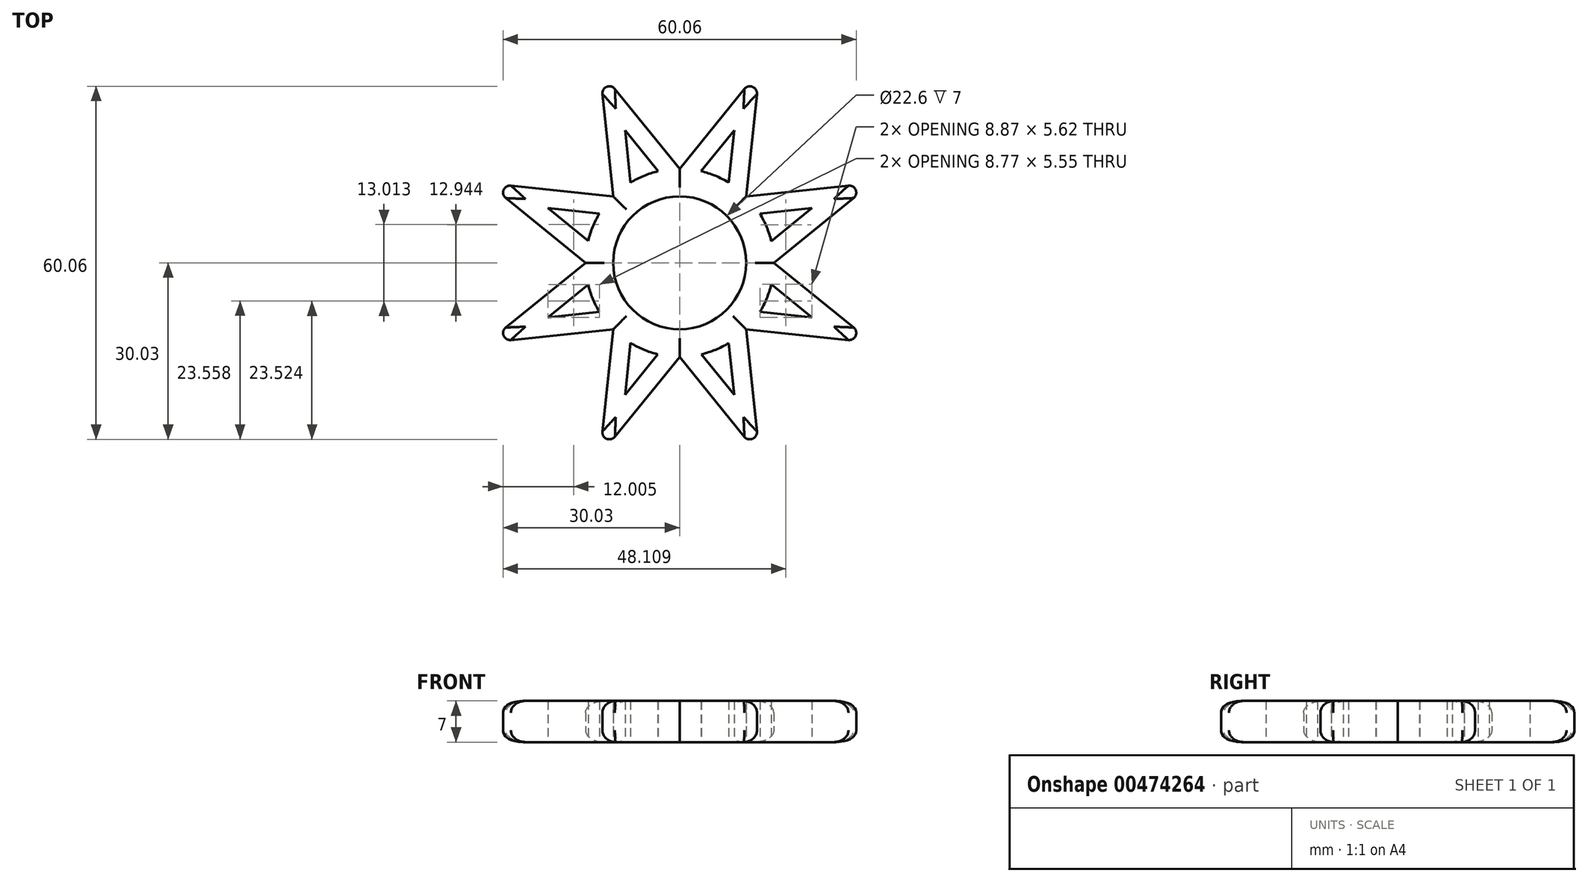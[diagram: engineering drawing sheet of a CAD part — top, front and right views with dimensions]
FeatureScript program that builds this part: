
annotation { "Feature Type Name" : "Feature", "Feature Type Description" : "" }
export const myFeature = defineFeature(function(context is Context, id is Id, definition is map)
    precondition{}
    {
        {
            var Q0;
            Q0=qCreatedBy(makeId("Top.planeOp"),FACE);
            var sketch = newSketch(context, id + "F0", { "sketchPlane" : qUnion([Q0])});
            skCircle(sketch, "E0", {"center": v(0, 0) * mm, "radius": 11.3 * mm});
            skCircle(sketch, "E1", {"center": v(0, 0) * mm, "radius": 16 * mm});
            skCircle(sketch, "E2.cCircle", {"center": v(0, 0) * mm, "radius": 16 * mm, "construction": true});
            skLineSegment(sketch, "E2.0", {"start": v(6.63, -16) * mm, "end": v(-6.63, -16) * mm});
            skLineSegment(sketch, "E2.1", {"start": v(-6.63, -16) * mm, "end": v(-16, -6.63) * mm});
            skLineSegment(sketch, "E2.2", {"start": v(-16, -6.63) * mm, "end": v(-16, 6.63) * mm});
            skLineSegment(sketch, "E2.3", {"start": v(-16, 6.63) * mm, "end": v(-6.63, 16) * mm});
            skLineSegment(sketch, "E2.4", {"start": v(-6.63, 16) * mm, "end": v(6.63, 16) * mm});
            skLineSegment(sketch, "E2.5", {"start": v(6.63, 16) * mm, "end": v(16, 6.63) * mm});
            skLineSegment(sketch, "E2.6", {"start": v(16, 6.63) * mm, "end": v(16, -6.63) * mm});
            skLineSegment(sketch, "E2.7", {"start": v(16, -6.63) * mm, "end": v(6.63, -16) * mm});
            skPoint(sketch, "E2.0.midPoint", {"position": v(0, -16) * mm});
            skCircle(sketch, "E3.cCircle", {"center": v(0, 0) * mm, "radius": 32.73 * mm, "construction": true});
            skLineSegment(sketch, "E3.0", {"start": v(13.56, -32.73) * mm, "end": v(-13.56, -32.73) * mm});
            skLineSegment(sketch, "E3.1", {"start": v(-13.56, -32.73) * mm, "end": v(-32.73, -13.56) * mm});
            skLineSegment(sketch, "E3.2", {"start": v(-32.73, -13.56) * mm, "end": v(-32.73, 13.56) * mm});
            skLineSegment(sketch, "E3.3", {"start": v(-32.73, 13.56) * mm, "end": v(-13.56, 32.73) * mm});
            skLineSegment(sketch, "E3.4", {"start": v(-13.56, 32.73) * mm, "end": v(13.56, 32.73) * mm});
            skLineSegment(sketch, "E3.5", {"start": v(13.56, 32.73) * mm, "end": v(32.73, 13.56) * mm});
            skLineSegment(sketch, "E3.6", {"start": v(32.73, 13.56) * mm, "end": v(32.73, -13.56) * mm});
            skLineSegment(sketch, "E3.7", {"start": v(32.73, -13.56) * mm, "end": v(13.56, -32.73) * mm});
            skPoint(sketch, "E3.0.midPoint", {"position": v(0, -32.73) * mm});
            skLineSegment(sketch, "E4", {"start": v(0, 16) * mm, "end": v(13.56, 32.73) * mm});
            skLineSegment(sketch, "E5", {"start": v(13.56, 32.73) * mm, "end": v(11.31, 11.31) * mm});
            skLineSegment(sketch, "E6", {"start": v(11.31, 11.31) * mm, "end": v(32.73, 13.56) * mm});
            skLineSegment(sketch, "E7", {"start": v(32.73, 13.56) * mm, "end": v(16, 0) * mm});
            skLineSegment(sketch, "E8", {"start": v(16, 0) * mm, "end": v(32.73, -13.56) * mm});
            skLineSegment(sketch, "E9", {"start": v(32.73, -13.56) * mm, "end": v(11.31, -11.31) * mm});
            skLineSegment(sketch, "E10", {"start": v(11.31, -11.31) * mm, "end": v(13.56, -32.73) * mm});
            skLineSegment(sketch, "E11", {"start": v(13.56, -32.73) * mm, "end": v(0, -16) * mm});
            skLineSegment(sketch, "E12", {"start": v(0, -16) * mm, "end": v(-13.56, -32.73) * mm});
            skLineSegment(sketch, "E13", {"start": v(-11.31, -11.31) * mm, "end": v(-13.56, -32.73) * mm});
            skLineSegment(sketch, "E14", {"start": v(0, 16) * mm, "end": v(-13.56, 32.73) * mm});
            skLineSegment(sketch, "E15", {"start": v(-11.31, 11.31) * mm, "end": v(-13.56, 32.73) * mm});
            skLineSegment(sketch, "E16", {"start": v(-11.31, 11.31) * mm, "end": v(-32.73, 13.56) * mm});
            skLineSegment(sketch, "E17", {"start": v(-32.73, 13.56) * mm, "end": v(-16, 0) * mm});
            skLineSegment(sketch, "E18", {"start": v(-16, 0) * mm, "end": v(-32.73, -13.56) * mm});
            skLineSegment(sketch, "E19", {"start": v(-32.73, -13.56) * mm, "end": v(-11.31, -11.31) * mm});
            skCircle(sketch, "E20.cCircle", {"center": v(0, 0) * mm, "radius": 22.41 * mm, "construction": true});
            skLineSegment(sketch, "E20.0", {"start": v(9.28, -22.41) * mm, "end": v(-9.28, -22.41) * mm});
            skLineSegment(sketch, "E20.1", {"start": v(-9.28, -22.41) * mm, "end": v(-22.41, -9.28) * mm});
            skLineSegment(sketch, "E20.2", {"start": v(-22.41, -9.28) * mm, "end": v(-22.41, 9.28) * mm});
            skLineSegment(sketch, "E20.3", {"start": v(-22.41, 9.28) * mm, "end": v(-9.28, 22.41) * mm});
            skLineSegment(sketch, "E20.4", {"start": v(-9.28, 22.41) * mm, "end": v(9.28, 22.41) * mm});
            skLineSegment(sketch, "E20.5", {"start": v(9.28, 22.41) * mm, "end": v(22.41, 9.28) * mm});
            skLineSegment(sketch, "E20.6", {"start": v(22.41, 9.28) * mm, "end": v(22.41, -9.28) * mm});
            skLineSegment(sketch, "E20.7", {"start": v(22.41, -9.28) * mm, "end": v(9.28, -22.41) * mm});
            skPoint(sketch, "E20.0.midPoint", {"position": v(0, -22.41) * mm});
            skLineSegment(sketch, "E21", {"start": v(-1, 7.04) * mm, "end": v(-22.41, 9.28) * mm});
            skLineSegment(sketch, "E22", {"start": v(-22.41, 9.28) * mm, "end": v(-5.69, -4.27) * mm});
            skLineSegment(sketch, "E23", {"start": v(-5.69, 4.27) * mm, "end": v(-22.41, -9.28) * mm});
            skLineSegment(sketch, "E24", {"start": v(-22.41, -9.28) * mm, "end": v(-1, -7.04) * mm});
            skPoint(sketch, "E25.0.midPoint", {"position": v(4.27, -5.69) * mm});
            skLineSegment(sketch, "E26", {"start": v(4.27, -5.69) * mm, "end": v(-9.28, -22.41) * mm});
            skLineSegment(sketch, "E27", {"start": v(-7.04, -1) * mm, "end": v(-9.28, -22.41) * mm});
            skPoint(sketch, "E28.0.midPoint", {"position": v(-4.3, -5.69) * mm});
            skLineSegment(sketch, "E29", {"start": v(7.01, -1) * mm, "end": v(9.25, -22.41) * mm});
            skLineSegment(sketch, "E30", {"start": v(9.25, -22.41) * mm, "end": v(-4.3, -5.69) * mm});
            skLineSegment(sketch, "E31", {"start": v(5.79, 4.27) * mm, "end": v(22.51, -9.28) * mm});
            skLineSegment(sketch, "E32", {"start": v(22.51, -9.28) * mm, "end": v(1.1, -7.04) * mm});
            skLineSegment(sketch, "E33", {"start": v(1.1, 7.04) * mm, "end": v(22.51, 9.28) * mm});
            skLineSegment(sketch, "E34", {"start": v(22.51, 9.28) * mm, "end": v(5.79, -4.27) * mm});
            skLineSegment(sketch, "E35", {"start": v(4.27, 5.78) * mm, "end": v(-9.28, 22.5) * mm});
            skLineSegment(sketch, "E36", {"start": v(-7.04, 1.1) * mm, "end": v(-9.28, 22.5) * mm});
            skLineSegment(sketch, "E37", {"start": v(-4.3, 5.78) * mm, "end": v(9.25, 22.5) * mm});
            skLineSegment(sketch, "E38", {"start": v(9.25, 22.5) * mm, "end": v(7.01, 1.1) * mm});
            skSolve(sketch);
        }
        {
            var Q0;
            Q0=makeQuery(id+"F0.imprint","IMPRINT",FACE,{"disambiguationData":[TD([[makeQuery(id+"F0.imprint","IMPRINT",EDGE,{"derivedFrom":sQuery(id+"F0.wireOp",EDGE,"E0")}),-1.0]])]});
            var Q1;
            {var subQ3=sQuery(id+"F0.wireOp",EDGE,"E4");Q1=makeQuery(id+"F0.imprint","IMPRINT",FACE,{"disambiguationData":[TD([[makeQuery(id+"F0.imprint","IMPRINT",EDGE,{"derivedFrom":subQ3}),-1.0]])]});}
            var Q2;
            {var subQ5=sQuery(id+"F0.wireOp",EDGE,"E14");Q2=makeQuery(id+"F0.imprint","IMPRINT",FACE,{"disambiguationData":[TD([[makeQuery(id+"F0.imprint","IMPRINT",EDGE,{"derivedFrom":subQ5}),1.0]])]});}
            var Q3;
            {var subQ5=sQuery(id+"F0.wireOp",EDGE,"E16");Q3=makeQuery(id+"F0.imprint","IMPRINT",FACE,{"disambiguationData":[TD([[makeQuery(id+"F0.imprint","IMPRINT",EDGE,{"derivedFrom":subQ5}),1.0]])]});}
            var Q4;
            {var subQ5=sQuery(id+"F0.wireOp",EDGE,"E18");Q4=makeQuery(id+"F0.imprint","IMPRINT",FACE,{"disambiguationData":[TD([[makeQuery(id+"F0.imprint","IMPRINT",EDGE,{"derivedFrom":subQ5}),1.0]])]});}
            var Q5;
            {var subQ3=sQuery(id+"F0.wireOp",EDGE,"E12");Q5=makeQuery(id+"F0.imprint","IMPRINT",FACE,{"disambiguationData":[TD([[makeQuery(id+"F0.imprint","IMPRINT",EDGE,{"derivedFrom":subQ3}),-1.0]])]});}
            var Q6;
            {var subQ5=sQuery(id+"F0.wireOp",EDGE,"E10");Q6=makeQuery(id+"F0.imprint","IMPRINT",FACE,{"disambiguationData":[TD([[makeQuery(id+"F0.imprint","IMPRINT",EDGE,{"derivedFrom":subQ5}),-1.0]])]});}
            var Q7;
            {var subQ3=sQuery(id+"F0.wireOp",EDGE,"E8");Q7=makeQuery(id+"F0.imprint","IMPRINT",FACE,{"disambiguationData":[TD([[makeQuery(id+"F0.imprint","IMPRINT",EDGE,{"derivedFrom":subQ3}),-1.0]])]});}
            var Q8;
            {var subQ3=sQuery(id+"F0.wireOp",EDGE,"E6");Q8=makeQuery(id+"F0.imprint","IMPRINT",FACE,{"disambiguationData":[TD([[makeQuery(id+"F0.imprint","IMPRINT",EDGE,{"derivedFrom":subQ3}),-1.0]])]});}
            var Q9;
            {var subQ1=sQuery(id+"F0.wireOp",EDGE,"E0");var subQ6=sQuery(id+"F0.wireOp",EDGE,"E36");var subQ8=makeQuery(id+"F0.imprint","INTERSECT",VERTEX,{"derivedFrom":[subQ1,subQ6]});Q9=makeQuery(id+"F0.imprint","IMPRINT",FACE,{"disambiguationData":[TD([[makeQuery(id+"F0.imprint","IMPRINT",EDGE,{"disambiguationData":[TD([[subQ8,-1.0]])],"derivedFrom":subQ1}),-1.0]])]});}
            var Q10;
            {var subQ4=sQuery(id+"F0.wireOp",EDGE,"E0");var subQ6=sQuery(id+"F0.wireOp",EDGE,"E37");var subQ8=makeQuery(id+"F0.imprint","INTERSECT",VERTEX,{"derivedFrom":[subQ4,subQ6]});Q10=makeQuery(id+"F0.imprint","IMPRINT",FACE,{"disambiguationData":[TD([[makeQuery(id+"F0.imprint","IMPRINT",EDGE,{"disambiguationData":[TD([[subQ8,-1.0]])],"derivedFrom":subQ4}),-1.0]])]});}
            var Q11;
            {var subQ0=sQuery(id+"F0.wireOp",EDGE,"E33");var subQ1=sQuery(id+"F0.wireOp",EDGE,"E0");var subQ2=makeQuery(id+"F0.imprint","INTERSECT",VERTEX,{"derivedFrom":[subQ1,subQ0]});Q11=makeQuery(id+"F0.imprint","IMPRINT",FACE,{"disambiguationData":[TD([[makeQuery(id+"F0.imprint","IMPRINT",EDGE,{"disambiguationData":[TD([[subQ2,-1.0]])],"derivedFrom":subQ1}),-1.0]])]});}
            var Q12;
            {var subQ1=sQuery(id+"F0.wireOp",EDGE,"E0");var subQ6=sQuery(id+"F0.wireOp",EDGE,"E34");var subQ8=makeQuery(id+"F0.imprint","INTERSECT",VERTEX,{"derivedFrom":[subQ1,subQ6]});Q12=makeQuery(id+"F0.imprint","IMPRINT",FACE,{"disambiguationData":[TD([[makeQuery(id+"F0.imprint","IMPRINT",EDGE,{"disambiguationData":[TD([[subQ8,1.0]])],"derivedFrom":subQ1}),-1.0]])]});}
            var Q13;
            {var subQ0=sQuery(id+"F0.wireOp",EDGE,"E29");var subQ1=sQuery(id+"F0.wireOp",EDGE,"E0");var subQ2=makeQuery(id+"F0.imprint","INTERSECT",VERTEX,{"derivedFrom":[subQ1,subQ0]});Q13=makeQuery(id+"F0.imprint","IMPRINT",FACE,{"disambiguationData":[TD([[makeQuery(id+"F0.imprint","IMPRINT",EDGE,{"disambiguationData":[TD([[subQ2,-1.0]])],"derivedFrom":subQ1}),-1.0]])]});}
            var Q14;
            {var subQ0=sQuery(id+"F0.wireOp",EDGE,"E26");var subQ1=sQuery(id+"F0.wireOp",EDGE,"E0");var subQ2=makeQuery(id+"F0.imprint","INTERSECT",VERTEX,{"derivedFrom":[subQ1,subQ0]});Q14=makeQuery(id+"F0.imprint","IMPRINT",FACE,{"disambiguationData":[TD([[makeQuery(id+"F0.imprint","IMPRINT",EDGE,{"disambiguationData":[TD([[subQ2,-1.0]])],"derivedFrom":subQ1}),-1.0]])]});}
            var Q15;
            {var subQ0=sQuery(id+"F0.wireOp",EDGE,"E24");var subQ1=sQuery(id+"F0.wireOp",EDGE,"E0");var subQ2=makeQuery(id+"F0.imprint","INTERSECT",VERTEX,{"derivedFrom":[subQ1,subQ0]});Q15=makeQuery(id+"F0.imprint","IMPRINT",FACE,{"disambiguationData":[TD([[makeQuery(id+"F0.imprint","IMPRINT",EDGE,{"disambiguationData":[TD([[subQ2,-1.0]])],"derivedFrom":subQ1}),-1.0]])]});}
            var Q16;
            {var subQ4=sQuery(id+"F0.wireOp",EDGE,"E22");var subQ5=sQuery(id+"F0.wireOp",EDGE,"E0");var subQ6=makeQuery(id+"F0.imprint","INTERSECT",VERTEX,{"derivedFrom":[subQ5,subQ4]});Q16=makeQuery(id+"F0.imprint","IMPRINT",FACE,{"disambiguationData":[TD([[makeQuery(id+"F0.imprint","IMPRINT",EDGE,{"disambiguationData":[TD([[subQ6,-1.0]])],"derivedFrom":subQ5}),-1.0]])]});}
            var Q17;
            {var subQ1=sQuery(id+"F0.wireOp",EDGE,"E1");var subQ3=sQuery(id+"F0.wireOp",EDGE,"E22");var subQ4=makeQuery(id+"F0.imprint","INTERSECT",VERTEX,{"derivedFrom":[subQ1,subQ3]});Q17=makeQuery(id+"F0.imprint","IMPRINT",FACE,{"disambiguationData":[TD([[makeQuery(id+"F0.imprint","IMPRINT",EDGE,{"disambiguationData":[TD([[subQ4,1.0]])],"derivedFrom":subQ3}),-1.0]])]});}
            var Q18;
            {var subQ1=sQuery(id+"F0.wireOp",EDGE,"E1");var subQ3=sQuery(id+"F0.wireOp",EDGE,"E21");var subQ4=makeQuery(id+"F0.imprint","INTERSECT",VERTEX,{"derivedFrom":[subQ1,subQ3]});Q18=makeQuery(id+"F0.imprint","IMPRINT",FACE,{"disambiguationData":[TD([[makeQuery(id+"F0.imprint","IMPRINT",EDGE,{"disambiguationData":[TD([[subQ4,-1.0]])],"derivedFrom":subQ3}),-1.0]])]});}
            var Q19;
            {var subQ1=sQuery(id+"F0.wireOp",EDGE,"E1");var subQ3=sQuery(id+"F0.wireOp",EDGE,"E36");var subQ4=makeQuery(id+"F0.imprint","INTERSECT",VERTEX,{"derivedFrom":[subQ1,subQ3]});Q19=makeQuery(id+"F0.imprint","IMPRINT",FACE,{"disambiguationData":[TD([[makeQuery(id+"F0.imprint","IMPRINT",EDGE,{"disambiguationData":[TD([[subQ4,-1.0]])],"derivedFrom":subQ3}),1.0]])]});}
            var Q20;
            {var subQ1=sQuery(id+"F0.wireOp",EDGE,"E1");var subQ3=sQuery(id+"F0.wireOp",EDGE,"E35");var subQ4=makeQuery(id+"F0.imprint","INTERSECT",VERTEX,{"derivedFrom":[subQ1,subQ3]});Q20=makeQuery(id+"F0.imprint","IMPRINT",FACE,{"disambiguationData":[TD([[makeQuery(id+"F0.imprint","IMPRINT",EDGE,{"disambiguationData":[TD([[subQ4,-1.0]])],"derivedFrom":subQ3}),-1.0]])]});}
            var Q21;
            {var subQ1=sQuery(id+"F0.wireOp",EDGE,"E1");var subQ3=sQuery(id+"F0.wireOp",EDGE,"E37");var subQ4=makeQuery(id+"F0.imprint","INTERSECT",VERTEX,{"derivedFrom":[subQ1,subQ3]});Q21=makeQuery(id+"F0.imprint","IMPRINT",FACE,{"disambiguationData":[TD([[makeQuery(id+"F0.imprint","IMPRINT",EDGE,{"disambiguationData":[TD([[subQ4,-1.0]])],"derivedFrom":subQ3}),1.0]])]});}
            var Q22;
            {var subQ1=sQuery(id+"F0.wireOp",EDGE,"E1");var subQ3=sQuery(id+"F0.wireOp",EDGE,"E38");var subQ4=makeQuery(id+"F0.imprint","INTERSECT",VERTEX,{"derivedFrom":[subQ1,subQ3]});Q22=makeQuery(id+"F0.imprint","IMPRINT",FACE,{"disambiguationData":[TD([[makeQuery(id+"F0.imprint","IMPRINT",EDGE,{"disambiguationData":[TD([[subQ4,1.0]])],"derivedFrom":subQ3}),1.0]])]});}
            var Q23;
            {var subQ0=sQuery(id+"F0.wireOp",EDGE,"E20.5");var subQ1=sQuery(id+"F0.wireOp",EDGE,"E20.4");var subQ2=makeQuery(id+"F0.imprint","INTERSECT",VERTEX,{"derivedFrom":[subQ1,subQ0]});Q23=makeQuery(id+"F0.imprint","IMPRINT",FACE,{"disambiguationData":[TD([[makeQuery(id+"F0.imprint","IMPRINT",EDGE,{"disambiguationData":[TD([[subQ2,1.0]])],"derivedFrom":subQ1}),-1.0]])]});}
            var Q24;
            {var subQ1=sQuery(id+"F0.wireOp",EDGE,"E1");var subQ3=sQuery(id+"F0.wireOp",EDGE,"E33");var subQ4=makeQuery(id+"F0.imprint","INTERSECT",VERTEX,{"derivedFrom":[subQ1,subQ3]});Q24=makeQuery(id+"F0.imprint","IMPRINT",FACE,{"disambiguationData":[TD([[makeQuery(id+"F0.imprint","IMPRINT",EDGE,{"disambiguationData":[TD([[subQ4,-1.0]])],"derivedFrom":subQ3}),1.0]])]});}
            var Q25;
            {var subQ1=sQuery(id+"F0.wireOp",EDGE,"E1");var subQ3=sQuery(id+"F0.wireOp",EDGE,"E34");var subQ4=makeQuery(id+"F0.imprint","INTERSECT",VERTEX,{"derivedFrom":[subQ1,subQ3]});Q25=makeQuery(id+"F0.imprint","IMPRINT",FACE,{"disambiguationData":[TD([[makeQuery(id+"F0.imprint","IMPRINT",EDGE,{"disambiguationData":[TD([[subQ4,1.0]])],"derivedFrom":subQ3}),1.0]])]});}
            var Q26;
            {var subQ1=sQuery(id+"F0.wireOp",EDGE,"E1");var subQ3=sQuery(id+"F0.wireOp",EDGE,"E31");var subQ4=makeQuery(id+"F0.imprint","INTERSECT",VERTEX,{"derivedFrom":[subQ1,subQ3]});Q26=makeQuery(id+"F0.imprint","IMPRINT",FACE,{"disambiguationData":[TD([[makeQuery(id+"F0.imprint","IMPRINT",EDGE,{"disambiguationData":[TD([[subQ4,-1.0]])],"derivedFrom":subQ3}),1.0]])]});}
            var Q27;
            {var subQ1=sQuery(id+"F0.wireOp",EDGE,"E1");var subQ3=sQuery(id+"F0.wireOp",EDGE,"E32");var subQ4=makeQuery(id+"F0.imprint","INTERSECT",VERTEX,{"derivedFrom":[subQ1,subQ3]});Q27=makeQuery(id+"F0.imprint","IMPRINT",FACE,{"disambiguationData":[TD([[makeQuery(id+"F0.imprint","IMPRINT",EDGE,{"disambiguationData":[TD([[subQ4,1.0]])],"derivedFrom":subQ3}),1.0]])]});}
            var Q28;
            {var subQ1=sQuery(id+"F0.wireOp",EDGE,"E1");var subQ3=sQuery(id+"F0.wireOp",EDGE,"E29");var subQ4=makeQuery(id+"F0.imprint","INTERSECT",VERTEX,{"derivedFrom":[subQ1,subQ3]});Q28=makeQuery(id+"F0.imprint","IMPRINT",FACE,{"disambiguationData":[TD([[makeQuery(id+"F0.imprint","IMPRINT",EDGE,{"disambiguationData":[TD([[subQ4,-1.0]])],"derivedFrom":subQ3}),1.0]])]});}
            var Q29;
            {var subQ1=sQuery(id+"F0.wireOp",EDGE,"E1");var subQ3=sQuery(id+"F0.wireOp",EDGE,"E30");var subQ4=makeQuery(id+"F0.imprint","INTERSECT",VERTEX,{"derivedFrom":[subQ1,subQ3]});Q29=makeQuery(id+"F0.imprint","IMPRINT",FACE,{"disambiguationData":[TD([[makeQuery(id+"F0.imprint","IMPRINT",EDGE,{"disambiguationData":[TD([[subQ4,1.0]])],"derivedFrom":subQ3}),1.0]])]});}
            var Q30;
            {var subQ1=sQuery(id+"F0.wireOp",EDGE,"E1");var subQ3=sQuery(id+"F0.wireOp",EDGE,"E26");var subQ4=makeQuery(id+"F0.imprint","INTERSECT",VERTEX,{"derivedFrom":[subQ1,subQ3]});Q30=makeQuery(id+"F0.imprint","IMPRINT",FACE,{"disambiguationData":[TD([[makeQuery(id+"F0.imprint","IMPRINT",EDGE,{"disambiguationData":[TD([[subQ4,-1.0]])],"derivedFrom":subQ3}),1.0]])]});}
            var Q31;
            {var subQ1=sQuery(id+"F0.wireOp",EDGE,"E1");var subQ3=sQuery(id+"F0.wireOp",EDGE,"E27");var subQ4=makeQuery(id+"F0.imprint","INTERSECT",VERTEX,{"derivedFrom":[subQ1,subQ3]});Q31=makeQuery(id+"F0.imprint","IMPRINT",FACE,{"disambiguationData":[TD([[makeQuery(id+"F0.imprint","IMPRINT",EDGE,{"disambiguationData":[TD([[subQ4,-1.0]])],"derivedFrom":subQ3}),-1.0]])]});}
            var Q32;
            {var subQ1=sQuery(id+"F0.wireOp",EDGE,"E1");var subQ3=sQuery(id+"F0.wireOp",EDGE,"E24");var subQ4=makeQuery(id+"F0.imprint","INTERSECT",VERTEX,{"derivedFrom":[subQ1,subQ3]});Q32=makeQuery(id+"F0.imprint","IMPRINT",FACE,{"disambiguationData":[TD([[makeQuery(id+"F0.imprint","IMPRINT",EDGE,{"disambiguationData":[TD([[subQ4,1.0]])],"derivedFrom":subQ3}),-1.0]])]});}
            var Q33;
            {var subQ1=sQuery(id+"F0.wireOp",EDGE,"E1");var subQ3=sQuery(id+"F0.wireOp",EDGE,"E23");var subQ4=makeQuery(id+"F0.imprint","INTERSECT",VERTEX,{"derivedFrom":[subQ1,subQ3]});Q33=makeQuery(id+"F0.imprint","IMPRINT",FACE,{"disambiguationData":[TD([[makeQuery(id+"F0.imprint","IMPRINT",EDGE,{"disambiguationData":[TD([[subQ4,-1.0]])],"derivedFrom":subQ3}),-1.0]])]});}
            var Q34;
            {var subQ1=sQuery(id+"F0.wireOp",EDGE,"E2.1");var subQ3=sQuery(id+"F0.wireOp",EDGE,"E24");var subQ4=makeQuery(id+"F0.imprint","INTERSECT",VERTEX,{"derivedFrom":[subQ1,subQ3]});Q34=makeQuery(id+"F0.imprint","IMPRINT",FACE,{"disambiguationData":[TD([[makeQuery(id+"F0.imprint","IMPRINT",EDGE,{"disambiguationData":[TD([[subQ4,1.0]])],"derivedFrom":subQ1}),1.0]])]});}
            var Q35;
            {var subQ1=sQuery(id+"F0.wireOp",EDGE,"E2.1");var subQ3=sQuery(id+"F0.wireOp",EDGE,"E27");var subQ4=makeQuery(id+"F0.imprint","INTERSECT",VERTEX,{"derivedFrom":[subQ1,subQ3]});Q35=makeQuery(id+"F0.imprint","IMPRINT",FACE,{"disambiguationData":[TD([[makeQuery(id+"F0.imprint","IMPRINT",EDGE,{"disambiguationData":[TD([[subQ4,-1.0]])],"derivedFrom":subQ1}),1.0]])]});}
            var Q36;
            {var subQ0=sQuery(id+"F0.wireOp",EDGE,"E11");var subQ5=sQuery(id+"F0.wireOp",EDGE,"E20.0");var subQ6=makeQuery(id+"F0.imprint","INTERSECT",VERTEX,{"derivedFrom":[subQ0,subQ5]});Q36=makeQuery(id+"F0.imprint","IMPRINT",FACE,{"disambiguationData":[TD([[makeQuery(id+"F0.imprint","IMPRINT",EDGE,{"disambiguationData":[TD([[subQ6,1.0]])],"derivedFrom":subQ5}),-1.0]])]});}
            var Q37;
            {var subQ0=sQuery(id+"F0.wireOp",EDGE,"E20.7");var subQ1=sQuery(id+"F0.wireOp",EDGE,"E20.6");var subQ2=makeQuery(id+"F0.imprint","INTERSECT",VERTEX,{"derivedFrom":[subQ1,subQ0]});Q37=makeQuery(id+"F0.imprint","IMPRINT",FACE,{"disambiguationData":[TD([[makeQuery(id+"F0.imprint","IMPRINT",EDGE,{"disambiguationData":[TD([[subQ2,1.0]])],"derivedFrom":subQ1}),-1.0]])]});}
            var Q38;
            {var subQ0=sQuery(id+"F0.wireOp",EDGE,"E7");var subQ5=sQuery(id+"F0.wireOp",EDGE,"E20.6");var subQ6=makeQuery(id+"F0.imprint","INTERSECT",VERTEX,{"derivedFrom":[subQ0,subQ5]});Q38=makeQuery(id+"F0.imprint","IMPRINT",FACE,{"disambiguationData":[TD([[makeQuery(id+"F0.imprint","IMPRINT",EDGE,{"disambiguationData":[TD([[subQ6,1.0]])],"derivedFrom":subQ5}),-1.0]])]});}
            var Q39;
            {var subQ1=sQuery(id+"F0.wireOp",EDGE,"E2.2");var subQ3=sQuery(id+"F0.wireOp",EDGE,"E22");var subQ4=makeQuery(id+"F0.imprint","INTERSECT",VERTEX,{"derivedFrom":[subQ1,subQ3]});Q39=makeQuery(id+"F0.imprint","IMPRINT",FACE,{"disambiguationData":[TD([[makeQuery(id+"F0.imprint","IMPRINT",EDGE,{"disambiguationData":[TD([[subQ4,1.0]])],"derivedFrom":subQ1}),1.0]])]});}
            var Q40;
            {var subQ0=sQuery(id+"F0.wireOp",EDGE,"E20.4");var subQ1=sQuery(id+"F0.wireOp",EDGE,"E20.3");var subQ2=makeQuery(id+"F0.imprint","INTERSECT",VERTEX,{"derivedFrom":[subQ1,subQ0]});Q40=makeQuery(id+"F0.imprint","IMPRINT",FACE,{"disambiguationData":[TD([[makeQuery(id+"F0.imprint","IMPRINT",EDGE,{"disambiguationData":[TD([[subQ2,1.0]])],"derivedFrom":subQ1}),-1.0]])]});}
            var Q41;
            {var subQ0=sQuery(id+"F0.wireOp",EDGE,"E20.4");var subQ1=sQuery(id+"F0.wireOp",EDGE,"E20.3");var subQ2=makeQuery(id+"F0.imprint","INTERSECT",VERTEX,{"derivedFrom":[subQ1,subQ0]});Q41=makeQuery(id+"F0.imprint","IMPRINT",FACE,{"disambiguationData":[TD([[makeQuery(id+"F0.imprint","IMPRINT",EDGE,{"disambiguationData":[TD([[subQ2,1.0]])],"derivedFrom":subQ1}),1.0]])]});}
            var Q42;
            {var subQ0=sQuery(id+"F0.wireOp",EDGE,"E20.4");var subQ1=sQuery(id+"F0.wireOp",EDGE,"E4");var subQ2=makeQuery(id+"F0.imprint","INTERSECT",VERTEX,{"derivedFrom":[subQ1,subQ0]});Q42=makeQuery(id+"F0.imprint","IMPRINT",FACE,{"disambiguationData":[TD([[makeQuery(id+"F0.imprint","IMPRINT",EDGE,{"disambiguationData":[TD([[subQ2,-1.0]])],"derivedFrom":subQ0}),1.0]])]});}
            var Q43;
            {var subQ0=sQuery(id+"F0.wireOp",EDGE,"E20.6");var subQ1=sQuery(id+"F0.wireOp",EDGE,"E20.5");var subQ2=makeQuery(id+"F0.imprint","INTERSECT",VERTEX,{"derivedFrom":[subQ1,subQ0]});Q43=makeQuery(id+"F0.imprint","IMPRINT",FACE,{"disambiguationData":[TD([[makeQuery(id+"F0.imprint","IMPRINT",EDGE,{"disambiguationData":[TD([[subQ2,1.0]])],"derivedFrom":subQ1}),1.0]])]});}
            var Q44;
            {var subQ1=sQuery(id+"F0.wireOp",EDGE,"E20.6");var subQ6=sQuery(id+"F0.wireOp",EDGE,"E8");var subQ9=makeQuery(id+"F0.imprint","INTERSECT",VERTEX,{"derivedFrom":[subQ6,subQ1]});Q44=makeQuery(id+"F0.imprint","IMPRINT",FACE,{"disambiguationData":[TD([[makeQuery(id+"F0.imprint","IMPRINT",EDGE,{"disambiguationData":[TD([[subQ9,-1.0]])],"derivedFrom":subQ1}),1.0]])]});}
            extrude(context, id + "F1", {"entities" : qUnion([Q0, Q1, Q2, Q3, Q4, Q5, Q6, Q7, Q8, Q9, Q10, Q11, Q12, Q13, Q14, Q15, Q16, Q17, Q18, Q19, Q20, Q21, Q22, Q23, Q24, Q25, Q26, Q27, Q28, Q29, Q30, Q31, Q32, Q33, Q34, Q35, Q36, Q37, Q38, Q39, Q40, Q41, Q42, Q43, Q44]), "depth" : 7 * mm});
        }
        {
            var Q0;
            Q0=makeQuery(id+"F1.opExtrude","CAP_EDGE",EDGE,{"disambiguationData":[OSD([sQuery(id+"F0.wireOp",EDGE,"E9")])],"isStart":false});
            var Q1;
            Q1=makeQuery(id+"F1.opExtrude","CAP_EDGE",EDGE,{"disambiguationData":[OSD([sQuery(id+"F0.wireOp",EDGE,"E10")])],"isStart":false});
            var Q2;
            Q2=makeQuery(id+"F1.opExtrude","CAP_EDGE",EDGE,{"disambiguationData":[OSD([sQuery(id+"F0.wireOp",EDGE,"E11")])],"isStart":false});
            var Q3;
            Q3=makeQuery(id+"F1.opExtrude","CAP_EDGE",EDGE,{"disambiguationData":[OSD([sQuery(id+"F0.wireOp",EDGE,"E12")])],"isStart":false});
            var Q4;
            Q4=makeQuery(id+"F1.opExtrude","CAP_EDGE",EDGE,{"disambiguationData":[OSD([sQuery(id+"F0.wireOp",EDGE,"E13")])],"isStart":false});
            var Q5;
            Q5=makeQuery(id+"F1.opExtrude","CAP_EDGE",EDGE,{"disambiguationData":[OSD([sQuery(id+"F0.wireOp",EDGE,"E19")])],"isStart":false});
            var Q6;
            Q6=makeQuery(id+"F1.opExtrude","CAP_EDGE",EDGE,{"disambiguationData":[OSD([sQuery(id+"F0.wireOp",EDGE,"E18")])],"isStart":false});
            var Q7;
            Q7=makeQuery(id+"F1.opExtrude","CAP_EDGE",EDGE,{"disambiguationData":[OSD([sQuery(id+"F0.wireOp",EDGE,"E17")])],"isStart":false});
            var Q8;
            Q8=makeQuery(id+"F1.opExtrude","CAP_EDGE",EDGE,{"disambiguationData":[OSD([sQuery(id+"F0.wireOp",EDGE,"E16")])],"isStart":false});
            var Q9;
            Q9=makeQuery(id+"F1.opExtrude","CAP_EDGE",EDGE,{"disambiguationData":[OSD([sQuery(id+"F0.wireOp",EDGE,"E15")])],"isStart":false});
            var Q10;
            Q10=makeQuery(id+"F1.opExtrude","CAP_EDGE",EDGE,{"disambiguationData":[OSD([sQuery(id+"F0.wireOp",EDGE,"E14")])],"isStart":false});
            var Q11;
            Q11=makeQuery(id+"F1.opExtrude","CAP_EDGE",EDGE,{"disambiguationData":[OSD([sQuery(id+"F0.wireOp",EDGE,"E4")])],"isStart":false});
            var Q12;
            Q12=makeQuery(id+"F1.opExtrude","CAP_EDGE",EDGE,{"disambiguationData":[OSD([sQuery(id+"F0.wireOp",EDGE,"E5")])],"isStart":false});
            var Q13;
            Q13=makeQuery(id+"F1.opExtrude","CAP_EDGE",EDGE,{"disambiguationData":[OSD([sQuery(id+"F0.wireOp",EDGE,"E6")])],"isStart":false});
            var Q14;
            Q14=makeQuery(id+"F1.opExtrude","CAP_EDGE",EDGE,{"disambiguationData":[OSD([sQuery(id+"F0.wireOp",EDGE,"E7")])],"isStart":false});
            var Q15;
            Q15=makeQuery(id+"F1.opExtrude","CAP_EDGE",EDGE,{"disambiguationData":[OSD([sQuery(id+"F0.wireOp",EDGE,"E8")])],"isStart":false});
            fillet(context, id + "F2", {"entities" : qUnion([Q0, Q1, Q2, Q3, Q4, Q5, Q6, Q7, Q8, Q9, Q10, Q11, Q12, Q13, Q14, Q15]), "radius" : 2 * mm, "tangentPropagation" : true, "allowEdgeOverflow" : false});
        }
        {
            var Q0;
            Q0=makeQuery(id+"F1.opExtrude","CAP_EDGE",EDGE,{"disambiguationData":[OSD([sQuery(id+"F0.wireOp",EDGE,"E12")])],"isStart":true});
            var Q1;
            Q1=makeQuery(id+"F1.opExtrude","CAP_EDGE",EDGE,{"disambiguationData":[OSD([sQuery(id+"F0.wireOp",EDGE,"E11")])],"isStart":true});
            var Q2;
            Q2=makeQuery(id+"F1.opExtrude","CAP_EDGE",EDGE,{"disambiguationData":[OSD([sQuery(id+"F0.wireOp",EDGE,"E10")])],"isStart":true});
            var Q3;
            Q3=makeQuery(id+"F1.opExtrude","CAP_EDGE",EDGE,{"disambiguationData":[OSD([sQuery(id+"F0.wireOp",EDGE,"E9")])],"isStart":true});
            var Q4;
            Q4=makeQuery(id+"F1.opExtrude","CAP_EDGE",EDGE,{"disambiguationData":[OSD([sQuery(id+"F0.wireOp",EDGE,"E8")])],"isStart":true});
            var Q5;
            Q5=makeQuery(id+"F1.opExtrude","CAP_EDGE",EDGE,{"disambiguationData":[OSD([sQuery(id+"F0.wireOp",EDGE,"E7")])],"isStart":true});
            var Q6;
            Q6=makeQuery(id+"F1.opExtrude","CAP_EDGE",EDGE,{"disambiguationData":[OSD([sQuery(id+"F0.wireOp",EDGE,"E6")])],"isStart":true});
            var Q7;
            Q7=makeQuery(id+"F1.opExtrude","CAP_EDGE",EDGE,{"disambiguationData":[OSD([sQuery(id+"F0.wireOp",EDGE,"E5")])],"isStart":true});
            var Q8;
            Q8=makeQuery(id+"F1.opExtrude","CAP_EDGE",EDGE,{"disambiguationData":[OSD([sQuery(id+"F0.wireOp",EDGE,"E4")])],"isStart":true});
            var Q9;
            Q9=makeQuery(id+"F1.opExtrude","CAP_EDGE",EDGE,{"disambiguationData":[OSD([sQuery(id+"F0.wireOp",EDGE,"E14")])],"isStart":true});
            var Q10;
            Q10=makeQuery(id+"F1.opExtrude","CAP_EDGE",EDGE,{"disambiguationData":[OSD([sQuery(id+"F0.wireOp",EDGE,"E15")])],"isStart":true});
            var Q11;
            Q11=makeQuery(id+"F1.opExtrude","CAP_EDGE",EDGE,{"disambiguationData":[OSD([sQuery(id+"F0.wireOp",EDGE,"E16")])],"isStart":true});
            var Q12;
            Q12=makeQuery(id+"F1.opExtrude","CAP_EDGE",EDGE,{"disambiguationData":[OSD([sQuery(id+"F0.wireOp",EDGE,"E17")])],"isStart":true});
            var Q13;
            Q13=makeQuery(id+"F1.opExtrude","CAP_EDGE",EDGE,{"disambiguationData":[OSD([sQuery(id+"F0.wireOp",EDGE,"E18")])],"isStart":true});
            var Q14;
            Q14=makeQuery(id+"F1.opExtrude","CAP_EDGE",EDGE,{"disambiguationData":[OSD([sQuery(id+"F0.wireOp",EDGE,"E19")])],"isStart":true});
            var Q15;
            Q15=makeQuery(id+"F1.opExtrude","CAP_EDGE",EDGE,{"disambiguationData":[OSD([sQuery(id+"F0.wireOp",EDGE,"E13")])],"isStart":true});
            fillet(context, id + "F3", {"entities" : qUnion([Q0, Q1, Q2, Q3, Q4, Q5, Q6, Q7, Q8, Q9, Q10, Q11, Q12, Q13, Q14, Q15]), "radius" : 2 * mm, "tangentPropagation" : true, "allowEdgeOverflow" : false});
        }
        {
            var Q0;
            Q0=makeQuery(id+"F1.opExtrude","SWEPT_EDGE",EDGE,{"disambiguationData":[OSD([sQuery(id+"F0.wireOp",EDGE,"E3.0"),sQuery(id+"F0.wireOp",EDGE,"E3.1"),sQuery(id+"F0.wireOp",EDGE,"E12"),sQuery(id+"F0.wireOp",EDGE,"E13")])]});
            var Q1;
            Q1=makeQuery(id+"F3.opFillet","BLEND_EDGE",EDGE,{"blendedFrom":[makeQuery(id+"F1.opExtrude","CAP_EDGE",EDGE,{"disambiguationData":[OSD([sQuery(id+"F0.wireOp",EDGE,"E12")])],"isStart":true}),makeQuery(id+"F1.opExtrude","CAP_EDGE",EDGE,{"disambiguationData":[OSD([sQuery(id+"F0.wireOp",EDGE,"E13")])],"isStart":true})],"blendedInto":[]});
            var Q2;
            Q2=makeQuery(id+"F2.opFillet","BLEND_EDGE",EDGE,{"blendedFrom":[makeQuery(id+"F1.opExtrude","CAP_EDGE",EDGE,{"disambiguationData":[OSD([sQuery(id+"F0.wireOp",EDGE,"E12")])],"isStart":false}),makeQuery(id+"F1.opExtrude","CAP_EDGE",EDGE,{"disambiguationData":[OSD([sQuery(id+"F0.wireOp",EDGE,"E13")])],"isStart":false})],"blendedInto":[]});
            var Q3;
            Q3=makeQuery(id+"F1.opExtrude","SWEPT_EDGE",EDGE,{"disambiguationData":[OSD([sQuery(id+"F0.wireOp",EDGE,"E3.0"),sQuery(id+"F0.wireOp",EDGE,"E3.7"),sQuery(id+"F0.wireOp",EDGE,"E10"),sQuery(id+"F0.wireOp",EDGE,"E11")])]});
            var Q4;
            Q4=makeQuery(id+"F2.opFillet","BLEND_EDGE",EDGE,{"blendedFrom":[makeQuery(id+"F1.opExtrude","CAP_EDGE",EDGE,{"disambiguationData":[OSD([sQuery(id+"F0.wireOp",EDGE,"E10")])],"isStart":false}),makeQuery(id+"F1.opExtrude","CAP_EDGE",EDGE,{"disambiguationData":[OSD([sQuery(id+"F0.wireOp",EDGE,"E11")])],"isStart":false})],"blendedInto":[]});
            var Q5;
            Q5=makeQuery(id+"F3.opFillet","BLEND_EDGE",EDGE,{"blendedFrom":[makeQuery(id+"F1.opExtrude","CAP_EDGE",EDGE,{"disambiguationData":[OSD([sQuery(id+"F0.wireOp",EDGE,"E10")])],"isStart":true}),makeQuery(id+"F1.opExtrude","CAP_EDGE",EDGE,{"disambiguationData":[OSD([sQuery(id+"F0.wireOp",EDGE,"E11")])],"isStart":true})],"blendedInto":[]});
            var Q6;
            Q6=makeQuery(id+"F2.opFillet","BLEND_EDGE",EDGE,{"blendedFrom":[makeQuery(id+"F1.opExtrude","CAP_EDGE",EDGE,{"disambiguationData":[OSD([sQuery(id+"F0.wireOp",EDGE,"E8")])],"isStart":false}),makeQuery(id+"F1.opExtrude","CAP_EDGE",EDGE,{"disambiguationData":[OSD([sQuery(id+"F0.wireOp",EDGE,"E9")])],"isStart":false})],"blendedInto":[]});
            var Q7;
            Q7=makeQuery(id+"F1.opExtrude","SWEPT_EDGE",EDGE,{"disambiguationData":[OSD([sQuery(id+"F0.wireOp",EDGE,"E3.6"),sQuery(id+"F0.wireOp",EDGE,"E3.7"),sQuery(id+"F0.wireOp",EDGE,"E8"),sQuery(id+"F0.wireOp",EDGE,"E9")])]});
            var Q8;
            Q8=makeQuery(id+"F3.opFillet","BLEND_EDGE",EDGE,{"blendedFrom":[makeQuery(id+"F1.opExtrude","CAP_EDGE",EDGE,{"disambiguationData":[OSD([sQuery(id+"F0.wireOp",EDGE,"E8")])],"isStart":true}),makeQuery(id+"F1.opExtrude","CAP_EDGE",EDGE,{"disambiguationData":[OSD([sQuery(id+"F0.wireOp",EDGE,"E9")])],"isStart":true})],"blendedInto":[]});
            var Q9;
            Q9=makeQuery(id+"F1.opExtrude","SWEPT_EDGE",EDGE,{"disambiguationData":[OSD([sQuery(id+"F0.wireOp",EDGE,"E3.5"),sQuery(id+"F0.wireOp",EDGE,"E3.6"),sQuery(id+"F0.wireOp",EDGE,"E6"),sQuery(id+"F0.wireOp",EDGE,"E7")])]});
            var Q10;
            Q10=makeQuery(id+"F2.opFillet","BLEND_EDGE",EDGE,{"blendedFrom":[makeQuery(id+"F1.opExtrude","CAP_EDGE",EDGE,{"disambiguationData":[OSD([sQuery(id+"F0.wireOp",EDGE,"E6")])],"isStart":false}),makeQuery(id+"F1.opExtrude","CAP_EDGE",EDGE,{"disambiguationData":[OSD([sQuery(id+"F0.wireOp",EDGE,"E7")])],"isStart":false})],"blendedInto":[]});
            var Q11;
            Q11=makeQuery(id+"F3.opFillet","BLEND_EDGE",EDGE,{"blendedFrom":[makeQuery(id+"F1.opExtrude","CAP_EDGE",EDGE,{"disambiguationData":[OSD([sQuery(id+"F0.wireOp",EDGE,"E6")])],"isStart":true}),makeQuery(id+"F1.opExtrude","CAP_EDGE",EDGE,{"disambiguationData":[OSD([sQuery(id+"F0.wireOp",EDGE,"E7")])],"isStart":true})],"blendedInto":[]});
            var Q12;
            Q12=makeQuery(id+"F2.opFillet","BLEND_EDGE",EDGE,{"blendedFrom":[makeQuery(id+"F1.opExtrude","CAP_EDGE",EDGE,{"disambiguationData":[OSD([sQuery(id+"F0.wireOp",EDGE,"E4")])],"isStart":false}),makeQuery(id+"F1.opExtrude","CAP_EDGE",EDGE,{"disambiguationData":[OSD([sQuery(id+"F0.wireOp",EDGE,"E5")])],"isStart":false})],"blendedInto":[]});
            var Q13;
            Q13=makeQuery(id+"F1.opExtrude","SWEPT_EDGE",EDGE,{"disambiguationData":[OSD([sQuery(id+"F0.wireOp",EDGE,"E3.4"),sQuery(id+"F0.wireOp",EDGE,"E3.5"),sQuery(id+"F0.wireOp",EDGE,"E4"),sQuery(id+"F0.wireOp",EDGE,"E5")])]});
            var Q14;
            Q14=makeQuery(id+"F3.opFillet","BLEND_EDGE",EDGE,{"blendedFrom":[makeQuery(id+"F1.opExtrude","CAP_EDGE",EDGE,{"disambiguationData":[OSD([sQuery(id+"F0.wireOp",EDGE,"E4")])],"isStart":true}),makeQuery(id+"F1.opExtrude","CAP_EDGE",EDGE,{"disambiguationData":[OSD([sQuery(id+"F0.wireOp",EDGE,"E5")])],"isStart":true})],"blendedInto":[]});
            var Q15;
            Q15=makeQuery(id+"F2.opFillet","BLEND_EDGE",EDGE,{"blendedFrom":[makeQuery(id+"F1.opExtrude","CAP_EDGE",EDGE,{"disambiguationData":[OSD([sQuery(id+"F0.wireOp",EDGE,"E14")])],"isStart":false}),makeQuery(id+"F1.opExtrude","CAP_EDGE",EDGE,{"disambiguationData":[OSD([sQuery(id+"F0.wireOp",EDGE,"E15")])],"isStart":false})],"blendedInto":[]});
            var Q16;
            Q16=makeQuery(id+"F1.opExtrude","SWEPT_EDGE",EDGE,{"disambiguationData":[OSD([sQuery(id+"F0.wireOp",EDGE,"E3.3"),sQuery(id+"F0.wireOp",EDGE,"E3.4"),sQuery(id+"F0.wireOp",EDGE,"E14"),sQuery(id+"F0.wireOp",EDGE,"E15")])]});
            var Q17;
            Q17=makeQuery(id+"F3.opFillet","BLEND_EDGE",EDGE,{"blendedFrom":[makeQuery(id+"F1.opExtrude","CAP_EDGE",EDGE,{"disambiguationData":[OSD([sQuery(id+"F0.wireOp",EDGE,"E14")])],"isStart":true}),makeQuery(id+"F1.opExtrude","CAP_EDGE",EDGE,{"disambiguationData":[OSD([sQuery(id+"F0.wireOp",EDGE,"E15")])],"isStart":true})],"blendedInto":[]});
            var Q18;
            Q18=makeQuery(id+"F2.opFillet","BLEND_EDGE",EDGE,{"blendedFrom":[makeQuery(id+"F1.opExtrude","CAP_EDGE",EDGE,{"disambiguationData":[OSD([sQuery(id+"F0.wireOp",EDGE,"E16")])],"isStart":false}),makeQuery(id+"F1.opExtrude","CAP_EDGE",EDGE,{"disambiguationData":[OSD([sQuery(id+"F0.wireOp",EDGE,"E17")])],"isStart":false})],"blendedInto":[]});
            var Q19;
            Q19=makeQuery(id+"F1.opExtrude","SWEPT_EDGE",EDGE,{"disambiguationData":[OSD([sQuery(id+"F0.wireOp",EDGE,"E3.2"),sQuery(id+"F0.wireOp",EDGE,"E3.3"),sQuery(id+"F0.wireOp",EDGE,"E16"),sQuery(id+"F0.wireOp",EDGE,"E17")])]});
            var Q20;
            Q20=makeQuery(id+"F3.opFillet","BLEND_EDGE",EDGE,{"blendedFrom":[makeQuery(id+"F1.opExtrude","CAP_EDGE",EDGE,{"disambiguationData":[OSD([sQuery(id+"F0.wireOp",EDGE,"E16")])],"isStart":true}),makeQuery(id+"F1.opExtrude","CAP_EDGE",EDGE,{"disambiguationData":[OSD([sQuery(id+"F0.wireOp",EDGE,"E17")])],"isStart":true})],"blendedInto":[]});
            var Q21;
            Q21=makeQuery(id+"F2.opFillet","BLEND_EDGE",EDGE,{"blendedFrom":[makeQuery(id+"F1.opExtrude","CAP_EDGE",EDGE,{"disambiguationData":[OSD([sQuery(id+"F0.wireOp",EDGE,"E18")])],"isStart":false}),makeQuery(id+"F1.opExtrude","CAP_EDGE",EDGE,{"disambiguationData":[OSD([sQuery(id+"F0.wireOp",EDGE,"E19")])],"isStart":false})],"blendedInto":[]});
            var Q22;
            Q22=makeQuery(id+"F1.opExtrude","SWEPT_EDGE",EDGE,{"disambiguationData":[OSD([sQuery(id+"F0.wireOp",EDGE,"E3.1"),sQuery(id+"F0.wireOp",EDGE,"E3.2"),sQuery(id+"F0.wireOp",EDGE,"E18"),sQuery(id+"F0.wireOp",EDGE,"E19")])]});
            var Q23;
            Q23=makeQuery(id+"F3.opFillet","BLEND_EDGE",EDGE,{"blendedFrom":[makeQuery(id+"F1.opExtrude","CAP_EDGE",EDGE,{"disambiguationData":[OSD([sQuery(id+"F0.wireOp",EDGE,"E18")])],"isStart":true}),makeQuery(id+"F1.opExtrude","CAP_EDGE",EDGE,{"disambiguationData":[OSD([sQuery(id+"F0.wireOp",EDGE,"E19")])],"isStart":true})],"blendedInto":[]});
            fillet(context, id + "F4", {"entities" : qUnion([Q0, Q1, Q2, Q3, Q4, Q5, Q6, Q7, Q8, Q9, Q10, Q11, Q12, Q13, Q14, Q15, Q16, Q17, Q18, Q19, Q20, Q21, Q22, Q23]), "radius" : 1.2 * mm, "tangentPropagation" : true, "allowEdgeOverflow" : false});
        }
    });
